# Revit family: Kombiventil 4206_M_SMART_LF_MF
name_source: partatom
category: Rohrzubehör
revit_build: Autodesk Revit 2018 (Build: 20190510_1515(x64)
units: mm (PartAtom-declared; Revit-internal decimal feet)

## family parameters
Arbeitsebenenbasiert = Nein
Beim Laden mit Abzugskörper schneiden = Nein
Bemaßung runder Anschluss = Durchmesser verwenden
Gemeinsam genutzt = Nein
Immer vertikal = Ja
OmniClass-Nummer = 23.65.55.14
OmniClass-Titel = Valves for Liquid Services
Teiletyp = Unterbricht

## types (2) — shared parameters
Anwendungsgebiet = Das Kombiventil wird in allen pumpenbetriebenen Heiz- und Kühlanlagen eingesetzt. Der Regler begrenzt automatisch
den Volumenstrom im gewählten Anlagenteil auf den einmal eingestellten Wert, indem alle Druckschwankungen
gemessen und ausgeregelt werden. Somit sind keine Messungen erforderlich und die Regelung ist bei allen
Betriebsbedingungen effektiv. Das Kombiventil regelt den Volumenstrom der ventileigenen Voreinstellung auf einen
konstanten Wert; die Membran regelt aufgrund des Druckes unmittelbar nach dem Regeleinsatz, sowie des Druckes
davor.
Die Voreinstellung bezieht sich direkt auf den Volumenstrom; entsprechend kann die maximale Durchflussmenge bei
der Montage direkt nach dem Diagramm eingestellt werden.
B01 = 41.62 mm  [stored 0.136549 ft]
B03 = 7.93 mm  [stored 0.0260171 ft]
B04 = 6.75 mm  [stored 0.0221457 ft]
B05 = 3.7 mm  [stored 0.0121391 ft]
B06 = 5.86 mm  [stored 0.0192257 ft]
B08 = 23.05 mm  [stored 0.0756234 ft]
B10 = 31.75 mm
B11 = 34.69 mm
B12 = 36.73 mm
B13 = 40.79 mm  [stored 0.133825 ft]
B14 = 8.73 mm  [stored 0.0286417 ft]
B15 = 23 mm  [stored 0.0754593 ft]
Bauschutzkappe = Kunststoff
Druckfeder = Federstahl
Gehäuse = DZR Messing CC770S
H01 = 35 mm  [stored 0.114829 ft]
H03 = 3.46 mm  [stored 0.0113517 ft]
H04 = 6.74 mm  [stored 0.0221129 ft]
H05 = 10.06 mm  [stored 0.0330052 ft]
H06 = 24.02 mm  [stored 0.0788058 ft]
H07 = 28.19 mm  [stored 0.0924869 ft]
H08 = 4.24 mm  [stored 0.0139108 ft]
H09 = 1.08 mm
H10 = 22.33 mm  [stored 0.0732612 ft]
Hersteller = Herz-Armaturen GmbH
Hub = 4 mm  [stored 0.0131234 ft]
Impulsleitung = Kupfer Cu-DHP (CW024A)
L01 = 41 mm  [stored 0.134514 ft]
L02 = 34 mm
L05 = 3.44 mm  [stored 0.0112861 ft]
L06 = 3.44 mm  [stored 0.0112861 ft]
Medium = Wasserbeschaffenheit nach ÖNORM H 5195 und VDI 2035.
Die Verwendung von Ethylen- und Propylenglykol ist im Mischungsverhältnis 25 - 50 Vol. [%] zulässig.
Membrane = EPDM
Membrangehäuse = Messing CW602N
O-Ringe = EPDM
PN = 25
SCRNCODE = 05;04;02
SCRNSEQ = ARM;ARM_TYP="DURR";2
Stift = Edelstahl 14301
URL = www.herz-armaturen.at
max.Betriebsdruck = 1600000.0 Pa
max.Betriebstemperatur ab DN40 = 110 °C
max.Betriebstemperatur bis DN32 = 130 °C
max.Differenzdruck = 400000.0 Pa
min.Betriebstemperatur (Frostschutz) = -20 °C
min.Betriebstemperatur (reines Wasser) = 2 °C

## type names (no varying parameters)
- LF
- MF

note: [stored X ft] marks values corroborated as IEEE doubles in the binary element streams (Revit-internal decimal feet)
